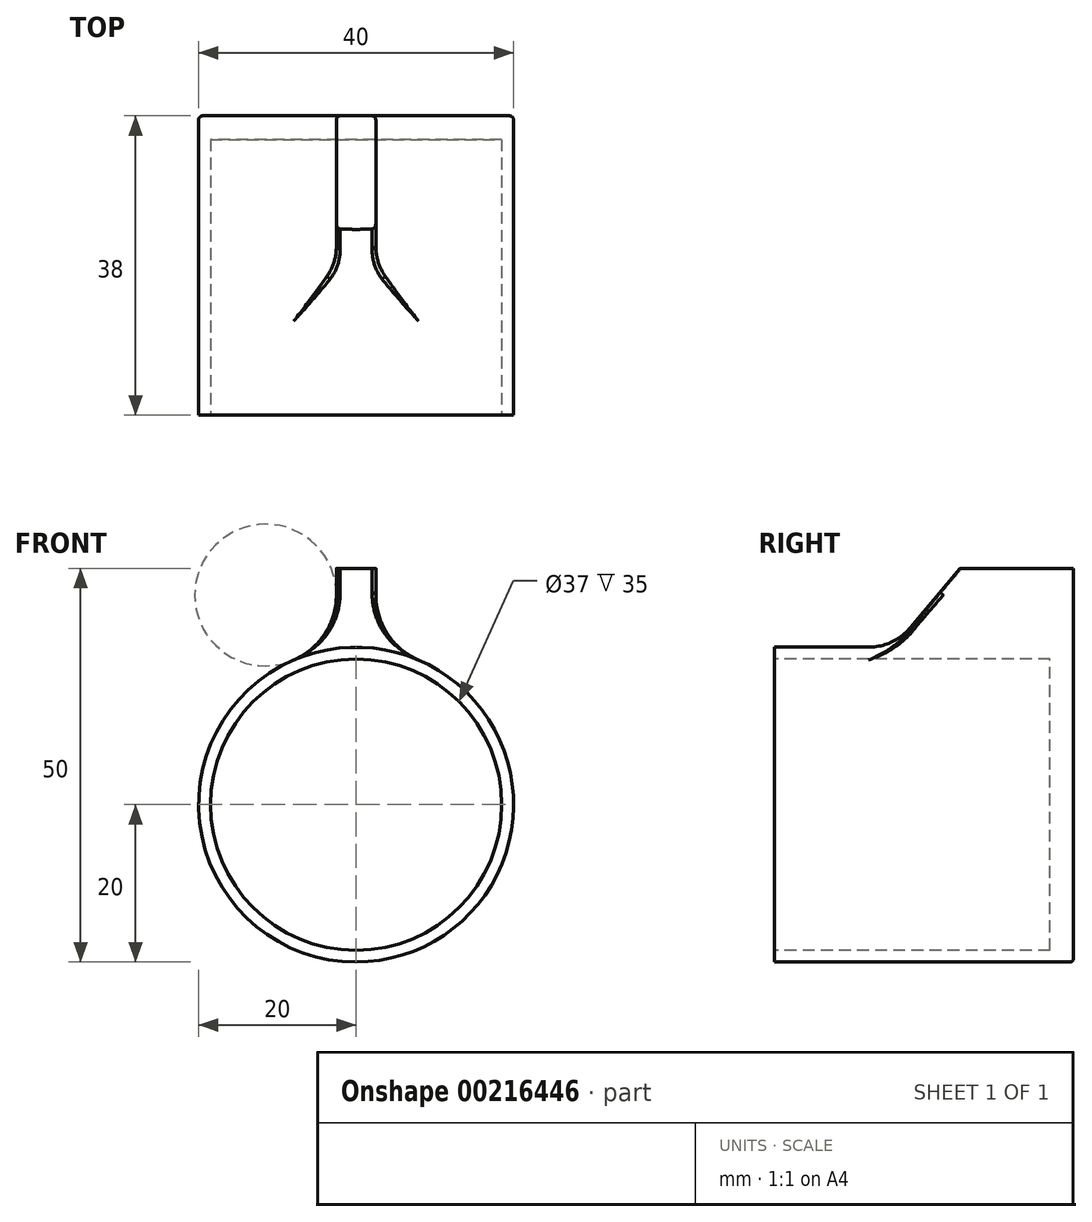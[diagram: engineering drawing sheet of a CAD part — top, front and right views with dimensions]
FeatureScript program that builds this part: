
annotation { "Feature Type Name" : "Feature", "Feature Type Description" : "" }
export const myFeature = defineFeature(function(context is Context, id is Id, definition is map)
    precondition{}
    {
        {
            var Q0;
            Q0=qCreatedBy(makeId("Front.planeOp"),FACE);
            var sketch = newSketch(context, id + "F0", { "sketchPlane" : qUnion([Q0])});
            skArc(sketch, "E0", {"start": v(-7.93, 18.36) * mm, "mid": v(0, -20) * mm, "end": v(7.93, 18.36) * mm});
            skLineSegment(sketch, "E1.bottom", {"start": v(-2.5, 30) * mm, "end": v(2.5, 30) * mm});
            skLineSegment(sketch, "E1.left", {"start": v(-2.5, 30) * mm, "end": v(-2.5, 26.62) * mm});
            skLineSegment(sketch, "E1.right", {"start": v(2.5, 30) * mm, "end": v(2.5, 26.62) * mm});
            skLineSegment(sketch, "E2", {"start": v(0, 45) * mm, "end": v(0, -25) * mm, "construction": true});
            skLineSegment(sketch, "E3", {"start": v(-10, -20) * mm, "end": v(10, -20) * mm, "construction": true});
            skArc(sketch, "E4", {"start": v(-7.93, 18.36) * mm, "mid": v(-3.98, 21.68) * mm, "end": v(-2.5, 26.62) * mm});
            skArc(sketch, "E5", {"start": v(2.5, 26.62) * mm, "mid": v(3.98, 21.68) * mm, "end": v(7.93, 18.36) * mm});
            skSolve(sketch);
        }
        {
            var Q0;
            Q0=makeQuery(id+"F0.imprint","IMPRINT",FACE,{"disambiguationData":[TD([[makeQuery(id+"F0.imprint","IMPRINT",EDGE,{"derivedFrom":sQuery(id+"F0.wireOp",EDGE,"E0")}),1.0]])]});
            extrude(context, id + "F1", {"entities" : qUnion([Q0]), "depth" : 38 * mm});
        }
        {
            var Q0;
            Q0=qCreatedBy(makeId("Right.planeOp"),FACE);
            var sketch = newSketch(context, id + "F2", { "sketchPlane" : qUnion([Q0])});
            skLineSegment(sketch, "E6", {"start": v(-14, 30.5) * mm, "end": v(-22.81, 20) * mm});
            skLineSegment(sketch, "E7", {"start": v(-22.81, 20) * mm, "end": v(-50, 20) * mm});
            skLineSegment(sketch, "E8", {"start": v(0, 0) * mm, "end": v(0, 38.42) * mm, "construction": true});
            skLineSegment(sketch, "E9", {"start": v(0, 0) * mm, "end": v(-57.1, 0) * mm, "construction": true});
            skLineSegment(sketch, "E10", {"start": v(-14, 30.5) * mm, "end": v(-14, 35) * mm});
            skLineSegment(sketch, "E11", {"start": v(-14, 35) * mm, "end": v(-50, 35) * mm});
            skLineSegment(sketch, "E12", {"start": v(-50, 35) * mm, "end": v(-50, 20) * mm});
            skLineSegment(sketch, "E13", {"start": v(-14, 30.5) * mm, "end": v(0, 30.5) * mm});
            skLineSegment(sketch, "E14", {"start": v(0, 30.5) * mm, "end": v(0, 35) * mm});
            skLineSegment(sketch, "E15", {"start": v(0, 35) * mm, "end": v(-14, 35) * mm});
            skSolve(sketch);
        }
        {
            var Q0;
            Q0=makeQuery(id+"F2.imprint","IMPRINT",FACE,{"disambiguationData":[TD([[makeQuery(id+"F2.imprint","IMPRINT",EDGE,{"derivedFrom":sQuery(id+"F2.wireOp",EDGE,"E6")}),-1.0]])]});
            var Q1;
            Q1=makeQuery(id+"F2.imprint","IMPRINT",FACE,{"disambiguationData":[TD([[makeQuery(id+"F2.imprint","IMPRINT",EDGE,{"derivedFrom":sQuery(id+"F2.wireOp",EDGE,"E10")}),-1.0]])]});
            var Q2;
            Q2=sQuery(id+"F2.wireOp",EDGE,"E9");
            revolve(context, id + "F3", {"operationType" : NewBodyOperationType.REMOVE, "entities" : qUnion([Q0, Q1]), "axis" : qUnion([Q2]), "revolveType" : RevolveType.FULL, "oppositeDirection" : true});
        }
        {
            var Q0;
            Q0=makeQuery(id+"F1.opExtrude","CAP_FACE",FACE,{"disambiguationData":[OSD([sQuery(id+"F0.wireOp",EDGE,"E0"),sQuery(id+"F0.wireOp",EDGE,"E1.bottom"),sQuery(id+"F0.wireOp",EDGE,"E1.left"),sQuery(id+"F0.wireOp",EDGE,"E1.right"),sQuery(id+"F0.wireOp",EDGE,"E4"),sQuery(id+"F0.wireOp",EDGE,"E5")])],"isStart":false});
            var sketch = newSketch(context, id + "F4", { "sketchPlane" : qUnion([Q0])});
            skCircle(sketch, "E16", {"center": v(0, 0) * mm, "radius": 18.5 * mm});
            skSolve(sketch);
        }
        {
            var Q0;
            Q0=makeQuery(id+"F4.imprint","IMPRINT",FACE,{"disambiguationData":[TD([[makeQuery(id+"F4.imprint","IMPRINT",EDGE,{"derivedFrom":sQuery(id+"F4.wireOp",EDGE,"E16")}),1.0]])]});
            extrude(context, id + "F5", {"entities" : qUnion([Q0]), "operationType" : NewBodyOperationType.REMOVE, "oppositeDirection" : true, "depth" : 35 * mm});
        }
        {
            var Q0;
            Q0=makeQuery(id+"F3.boolean.opBoolean","COPY",EDGE,{"derivedFrom":makeQuery(id+"F3.opRevolve","SWEPT_EDGE",EDGE,{"disambiguationData":[OSD([sQuery(id+"F2.wireOp",EDGE,"E6"),sQuery(id+"F2.wireOp",EDGE,"E7")])]})});
            fillet(context, id + "F6", {"entities" : qUnion([Q0]), "radius" : 7 * mm, "tangentPropagation" : true, "allowEdgeOverflow" : false});
        }
        {
            var Q0;
            Q0=makeQuery(id+"F3.boolean.opBoolean","INTERSECT",EDGE,{"derivedFrom":[makeQuery(id+"F1.opExtrude","SWEPT_FACE",FACE,{"disambiguationData":[OSD([sQuery(id+"F0.wireOp",EDGE,"E5")])]}),makeQuery(id+"F3.opRevolve","SWEPT_FACE",FACE,{"disambiguationData":[OSD([sQuery(id+"F2.wireOp",EDGE,"E6")])]})]});
            var Q1;
            Q1=makeQuery(id+"F6.opFillet","BLEND_EDGE",EDGE,{"blendedFrom":[makeQuery(id+"F3.boolean.opBoolean","COPY",EDGE,{"derivedFrom":makeQuery(id+"F3.opRevolve","SWEPT_EDGE",EDGE,{"disambiguationData":[OSD([sQuery(id+"F2.wireOp",EDGE,"E6"),sQuery(id+"F2.wireOp",EDGE,"E7")])]})}),makeQuery(id+"F1.opExtrude","SWEPT_FACE",FACE,{"disambiguationData":[OSD([sQuery(id+"F0.wireOp",EDGE,"E4")])]})],"blendedInto":[makeQuery(id+"F1.opExtrude","SWEPT_FACE",FACE,{"disambiguationData":[OSD([sQuery(id+"F0.wireOp",EDGE,"E4")])]})]});
            var Q2;
            Q2=makeQuery(id+"F3.boolean.opBoolean","COPY",FACE,{"derivedFrom":makeQuery(id+"F3.opRevolve","SWEPT_FACE",FACE,{"disambiguationData":[OSD([sQuery(id+"F2.wireOp",EDGE,"E13")])]})});
            var Q3;
            Q3=makeQuery(id+"F1.opExtrude","CAP_EDGE",EDGE,{"disambiguationData":[OSD([sQuery(id+"F0.wireOp",EDGE,"E5")])],"isStart":true});
            fillet(context, id + "F7", {"entities" : qUnion([Q0, Q1, Q2, Q3]), "radius" : 0.5 * mm, "tangentPropagation" : true, "allowEdgeOverflow" : false});
        }
    });
